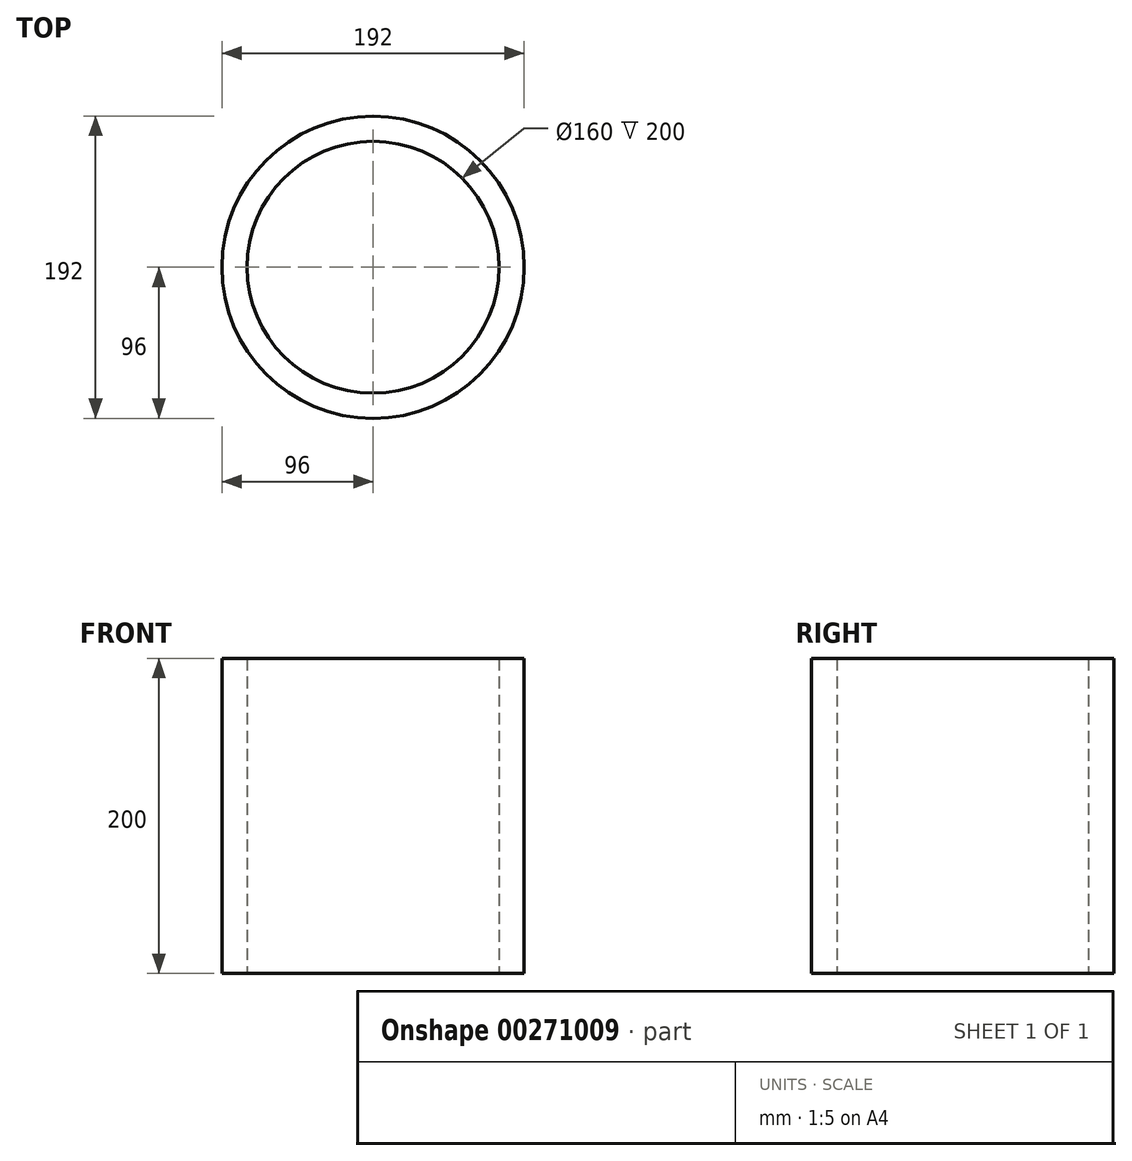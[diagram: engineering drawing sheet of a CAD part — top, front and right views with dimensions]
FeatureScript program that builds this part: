
annotation { "Feature Type Name" : "Feature", "Feature Type Description" : "" }
export const myFeature = defineFeature(function(context is Context, id is Id, definition is map)
    precondition{}
    {
        {
            var Q0;
            Q0=qCreatedBy(makeId("Front.planeOp"),FACE);
            var sketch = newSketch(context, id + "F0", { "sketchPlane" : qUnion([Q0])});
            skLineSegment(sketch, "E0.bottom", {"start": v(-80, 0) * mm, "end": v(-96, 0) * mm});
            skLineSegment(sketch, "E0.top", {"start": v(-80, 200) * mm, "end": v(-96, 200) * mm});
            skLineSegment(sketch, "E0.left", {"start": v(-80, 0) * mm, "end": v(-80, 200) * mm});
            skLineSegment(sketch, "E0.right", {"start": v(-96, 0) * mm, "end": v(-96, 200) * mm});
            skLineSegment(sketch, "E1", {"start": v(0, 0) * mm, "end": v(0, 212.96) * mm});
            skSolve(sketch);
        }
        {
            var Q0;
            Q0=makeQuery(id+"F0.imprint","IMPRINT",FACE,{"disambiguationData":[TD([[makeQuery(id+"F0.imprint","IMPRINT",EDGE,{"derivedFrom":sQuery(id+"F0.wireOp",EDGE,"E0.bottom")}),-1.0]])]});
            var Q1;
            Q1=sQuery(id+"F0.wireOp",EDGE,"E1");
            revolve(context, id + "F1", {"entities" : qUnion([Q0]), "axis" : qUnion([Q1]), "revolveType" : RevolveType.FULL});
        }
    });
